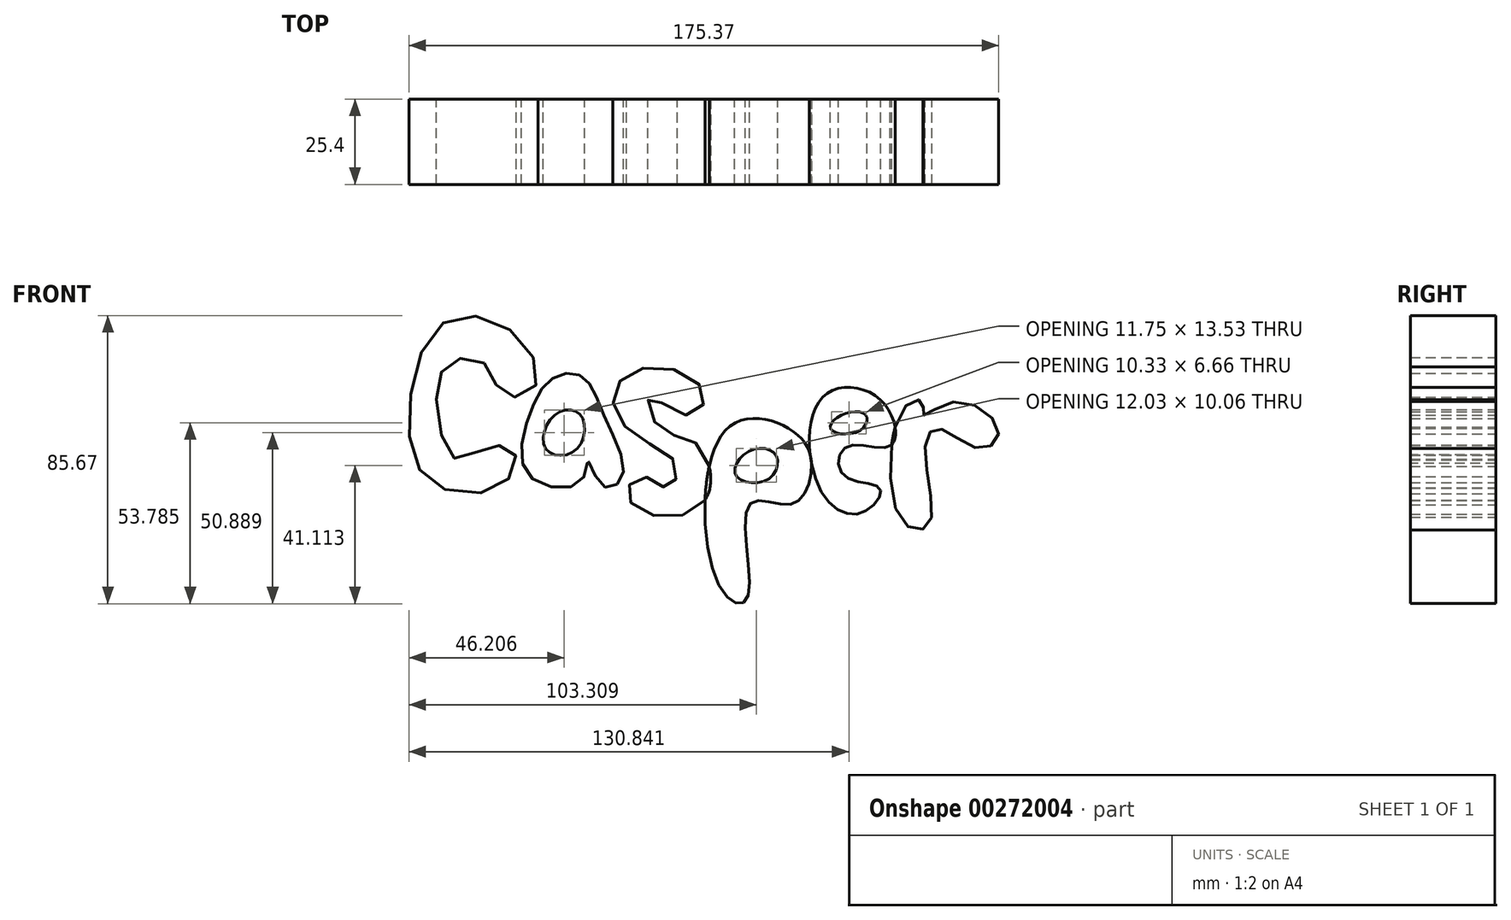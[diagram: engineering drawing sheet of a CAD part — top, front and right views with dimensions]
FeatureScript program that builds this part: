
annotation { "Feature Type Name" : "Feature", "Feature Type Description" : "" }
export const myFeature = defineFeature(function(context is Context, id is Id, definition is map)
    precondition{}
    {
        {
            var Q0;
            Q0=qCreatedBy(makeId("Front.planeOp"),FACE);
            var sketch = newSketch(context, id + "F0", { "sketchPlane" : qUnion([Q0])});
            skFitSpline(sketch, "E0", {"points": [v(-52, 15.53) * mm, v(-46.12, 6.12) * mm, v(-36.71, 8.7) * mm, v(-43.3, 24.47) * mm, v(-64, 27.53) * mm, v(-74.36, 0) * mm, v(-67.07, -20.47) * mm, v(-46.6, -20.7) * mm, v(-43.06, -11.06) * mm, v(-51.54, -9.65) * mm, v(-60.71, -12.94) * mm, v(-66.13, 3.53) * mm, v(-62.36, 15.53) * mm, v(-52, 15.53) * mm]});
            skPoint(sketch, "E1.2.internal.orphan", {"position": v(-38.6, 0) * mm});
            skPoint(sketch, "E1.8.internal.orphan", {"position": v(-16.47, 0) * mm});
            skFitSpline(sketch, "E2", {"points": [v(-16.47, 0) * mm, v(-22.6, 11.3) * mm, v(-31.06, 11.3) * mm, v(-38.6, 0) * mm, v(-38.6, -18.12) * mm, v(-23.06, -19.53) * mm, v(-21.18, -13.41) * mm, v(-16.47, -21.18) * mm, v(-10.82, -17.88) * mm, v(-16.47, 0) * mm]});
            skFitSpline(sketch, "E3", {"points": [v(-31.06, 0) * mm, v(-33.65, -10.12) * mm, v(-24.7, -10.35) * mm, v(-23.3, 0) * mm, v(-31.06, 0) * mm]});
            skFitSpline(sketch, "E4", {"points": [v(-2.82, 5.18) * mm, v(8, 0) * mm, v(13.65, 5.88) * mm, v(0, 14.35) * mm, v(-13.18, 7.77) * mm, v(-8.47, -4.94) * mm, v(5.18, -14.83) * mm, v(2.59, -21.65) * mm, v(-4.24, -18.36) * mm, v(-9.65, -23.06) * mm, v(0, -30.12) * mm, v(14.35, -24) * mm, v(11.06, -8.47) * mm, v(0, -3.77) * mm, v(-2.82, 5.18) * mm]});
            skFitSpline(sketch, "E5", {"points": [v(20.24, -4) * mm, v(18.6, -52) * mm, v(26.12, -54.6) * mm, v(26.83, -26.6) * mm, v(38.83, -26.6) * mm, v(44.95, -18.6) * mm, v(41.65, -6.35) * mm, v(20.24, -4) * mm]});
            skFitSpline(sketch, "E6", {"points": [v(26.6, -10.82) * mm, v(22.83, -17.88) * mm, v(32.47, -19.06) * mm, v(34.6, -11.77) * mm, v(26.6, -10.82) * mm]});
            skFitSpline(sketch, "E7", {"points": [v(55.77, -9.41) * mm, v(68.71, -9.18) * mm, v(66.36, 4) * mm, v(48.71, 5.41) * mm, v(48.24, -22.83) * mm, v(60.48, -28.94) * mm, v(65.66, -21.89) * mm, v(54.83, -17.88) * mm, v(55.77, -9.41) * mm]});
            skFitSpline(sketch, "E8", {"points": [v(54.12, 0) * mm, v(51.07, -4.24) * mm, v(59.54, -4.7) * mm, v(61.42, 0) * mm, v(54.12, 0) * mm]});
            skFitSpline(sketch, "E9", {"points": [v(72.71, 2.12) * mm, v(72.24, -31.53) * mm, v(80.25, -32.47) * mm, v(79.07, -10.82) * mm, v(82.83, -4) * mm, v(95.3, -9.88) * mm, v(100.95, -4.7) * mm, v(87.78, 4) * mm, v(78.6, 0) * mm, v(78.36, 3.77) * mm, v(72.71, 2.12) * mm]});
            skSolve(sketch);
        }
        {
            var Q0;
            Q0=makeQuery(id+"F0.imprint","IMPRINT",FACE,{"disambiguationData":[TD([[makeQuery(id+"F0.imprint","IMPRINT",EDGE,{"derivedFrom":sQuery(id+"F0.wireOp",EDGE,"E0")}),1.0]])]});
            var Q1;
            Q1=makeQuery(id+"F0.imprint","IMPRINT",FACE,{"disambiguationData":[TD([[makeQuery(id+"F0.imprint","IMPRINT",EDGE,{"derivedFrom":sQuery(id+"F0.wireOp",EDGE,"E2")}),1.0]])]});
            var Q2;
            {var subQ0=sQuery(id+"F0.wireOp",EDGE,"E5");var subQ1=sQuery(id+"F0.wireOp",EDGE,"E4");var subQ2=makeQuery(id+"F0.imprint","INTERSECT",VERTEX,{"disambiguationData":[OD(0.0)],"derivedFrom":[subQ1,subQ0]});Q2=makeQuery(id+"F0.imprint","IMPRINT",FACE,{"disambiguationData":[TD([[makeQuery(id+"F0.imprint","IMPRINT",EDGE,{"disambiguationData":[TD([[subQ2,1.0]])],"derivedFrom":subQ1}),1.0]])]});}
            var Q3;
            Q3=makeQuery(id+"F0.imprint","IMPRINT",FACE,{"disambiguationData":[TD([[makeQuery(id+"F0.imprint","IMPRINT",EDGE,{"derivedFrom":sQuery(id+"F0.wireOp",EDGE,"E6")}),-1.0]])]});
            var Q4;
            Q4=makeQuery(id+"F0.imprint","IMPRINT",FACE,{"disambiguationData":[TD([[makeQuery(id+"F0.imprint","IMPRINT",EDGE,{"derivedFrom":sQuery(id+"F0.wireOp",EDGE,"E8")}),-1.0]])]});
            var Q5;
            {var subQ0=sQuery(id+"F0.wireOp",EDGE,"E9");var subQ1=sQuery(id+"F0.wireOp",EDGE,"E7");var subQ2=makeQuery(id+"F0.imprint","INTERSECT",VERTEX,{"disambiguationData":[OD(0.0)],"derivedFrom":[subQ1,subQ0]});Q5=makeQuery(id+"F0.imprint","IMPRINT",FACE,{"disambiguationData":[TD([[makeQuery(id+"F0.imprint","IMPRINT",EDGE,{"disambiguationData":[TD([[subQ2,1.0]])],"derivedFrom":subQ1}),-1.0]])]});}
            extrude(context, id + "F1", {"entities" : qUnion([Q0, Q1, Q2, Q3, Q4, Q5]), "depth" : 25.4 * mm});
        }
    });
